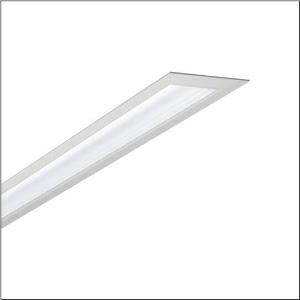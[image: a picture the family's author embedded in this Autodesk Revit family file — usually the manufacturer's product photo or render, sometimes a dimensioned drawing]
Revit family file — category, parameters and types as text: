
# Revit family: silica_r_5mx11bd2w4a_6c5b
name_source: partatom
category: Lighting Fixtures
units: mm (PartAtom-declared; Revit-internal decimal feet)

## family parameters
Cut with Voids When Loaded = No
Host = Face
Light Source = No
Part Type = Normal
Room Calculation Point = No
Round Connector Dimension = Use Diameter
Shared = No

## types (1)
- --- (1 x LED, 9910 lm, 60.1 W, 4000K)
    Apparent Load = 60 VA
    CIE Flux Codes = 82 97 100 100 100
    Color Rendering = 80
    Color Temperature = 4000K
    Default Elevation = 1800 mm
    Description = Silica®, office luminaire, of aluminium, light emission: direct distribution, primary light characteristic: symmetric, installation type: recessed, LED, rated luminous flux: 9.910lm, luminous efficacy: 165lm/W, light colour: 840, colour temperature: 4000K, control gear: ECG DALI, with terminal, 3+2-pole, max. 2.5mm², mains connection: 230V, AC, 50/60Hz, rated input power: 60W, luminaire housing, of aluminium, matt pure white (RAL 9010), length: 2.864mm, width: 93mm, height: 60mm, end cap, of diecast zinc, pure white (RAL 9010), protection rating (complete): IP20, insulation class (complete): insulation class I (protective earthing), certification: CE, permissible operating ambient temperature: 0..+35°C, standard: EN 50419, packaging unit: 1 piece
    Height = 0 mm  [stored 0 ft]
    Lamp = 1 x LED
    Lamp Light Flux = 9910 lm
    Lamp Power = 60.1 W
    Lamp count = 1
    Length = 2865 mm
    Luminous efficacy = 165 lm/W
    Manufacturer = Siteco
    ModVariant = No
    Model = 5MX11BD2W4A
    Mounting Place = Ceiling
    Mounting Type = Recessed
    Number of Poles = 1
    OnlyDefault = Yes
    Power Factor = 1
    Product Name = Silica®
    Product group = office luminaire | ceiling recessed
    ProductGroupID = 400
    Protection Class = Protection class I
    Protection Degree = IP 20
    RLX_Detail_Level = 1
    RLX_Emergency_Light_Flux = 0 lm
    RLX_Emergency_Type = 0
    RLX_Emergency_Type_DB = No
    RlxData = <blob elided: 24333 chars, md5=545a88e5>
    Socket = socket
    Standby Power = 0 W
    System Light Flux = 9910 lm
    System Power = 60 W
    Type Comments = factory setting: luminous flux: 100 % | dim-lin: 254 | 336 mA
    Type Image = l_1004825.jpg
    URL = http://relux.com
    VarID = @adj_173012
    Voltage = 0 V
    Weight = 0.00 kg
    Width = 93 mm

note: [stored X ft] marks values corroborated as IEEE doubles in the binary element streams (Revit-internal decimal feet)

## geometry (parser evidence)
native form markers: Blend x4, Sweep x12
no freeform markers — native parametric forms only
